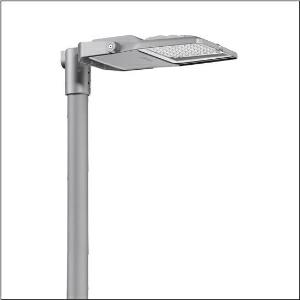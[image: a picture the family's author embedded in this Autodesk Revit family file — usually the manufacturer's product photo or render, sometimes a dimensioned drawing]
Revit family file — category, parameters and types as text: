
# Revit family: floodlight_fl_21_iq_mini___pl43_5xa7771b4a3a_ae81
name_source: partatom
category: Lighting Fixtures
units: mm (PartAtom-declared; Revit-internal decimal feet)

## family parameters
Cut with Voids When Loaded = No
Host = Face
Light Source = No
Part Type = Normal
Room Calculation Point = No
Round Connector Dimension = Use Diameter
Shared = No

## types (1)
- --- (1 x LED, 6660 lm, 45.5 W, 4000K)
    Apparent Load = 46 VA
    CIE Flux Codes = 27 78 99 100 100
    Color Rendering = 70
    Color Temperature = 4000K
    Default Elevation = 1800 mm
    Description = Floodlight FL 21 iQ mini, floodlight, primary light control with lens, of PMMA, primary optical cover: protective disc, of toughened safety glass, transparent, light distribution: PL43, light emission: direct distribution, installation type: surface-mounted, LED, High Power LED, rated luminous flux: 6.660lm, luminous efficacy: 146lm/W, light colour: 740, colour temperature: 4000K, control: Auto-Match, Temp-Guard, Lumen-Switch, Night-Set, Smart-Wire, Light-Fading, Desk-Remote (wireless, voltage-free reading and setting of iQ features in the workshop via application-optimized NFC function/RFID function), optimised constant luminous flux control (CLO 2.0), with terminal, 6-pole, mains connection: 220..240V, AC, 50/60Hz, start of lifetime: 46W, end of service life: 48W, reduction: 22W, luminaire housing, of diecast aluminium, powder-coated, Siteco® metallic grey (DB 702S), corrosivity category C5 mid according to DIN EN ISO 12944, sealing non-destructively replaceable, please order mast flange separately, mast bracket, of steel, galvanised, powder-coated, Siteco® metallic grey (DB 702S), protection rating (complete): IP66, insulation class (complete): insulation class II (safety insulation), certification: CE, ENEC, VDE, protection symbol: D, impact resistance: IK08, permissible operating ambient temperature: -40..+40°C, permissible operating ambient temperature for outdoor applications: -40..+50°C, standard: DIN EN 12944, LABS conformity tested according to VDMA 24364:2018-05, packaging unit: 1 piece

Light Distribution: PL43
    Height = 70 mm
    Lamp = 1 x LED
    Lamp Light Flux = 6660 lm
    Lamp Power = 45.5 W
    Lamp count = 1
    Length = 485 mm
    Luminous efficacy = 146 lm/W
    Manufacturer = Siteco
    ModVariant = No
    Model = 5XA7771B4A3A
    Number of Poles = 1
    OnlyDefault = Yes
    Power Factor = 1
    Product Name = Floodlight FL 21 iQ mini | PL43
    Product group = floodlight | pylon annexe
    ProductGroupID = 6200
    Protection Class = Protection class II
    Protection Degree = IP 66
    RLX_Detail_Level = 1
    RLX_Emergency_Light_Flux = 0 lm
    RLX_Emergency_Type = 0
    RLX_Emergency_Type_DB = No
    RlxData = <blob elided: 101041 chars, md5=bbfae750>
    Socket = socket
    Standby Power = 0 W
    System Light Flux = 6660 lm
    System Power = 46 W
    Type Comments = factory setting: luminous flux: 100 % | dim-lin: 254 | 463 mA
    Type Image = l_1007125.jpg
    URL = http://relux.com
    VarID = @adj_133231
    Voltage = 0 V
    Weight = 0.00 kg
    Width = 337 mm

## geometry (parser evidence)
native form markers: Blend x4, Sweep x14
no freeform markers — native parametric forms only
